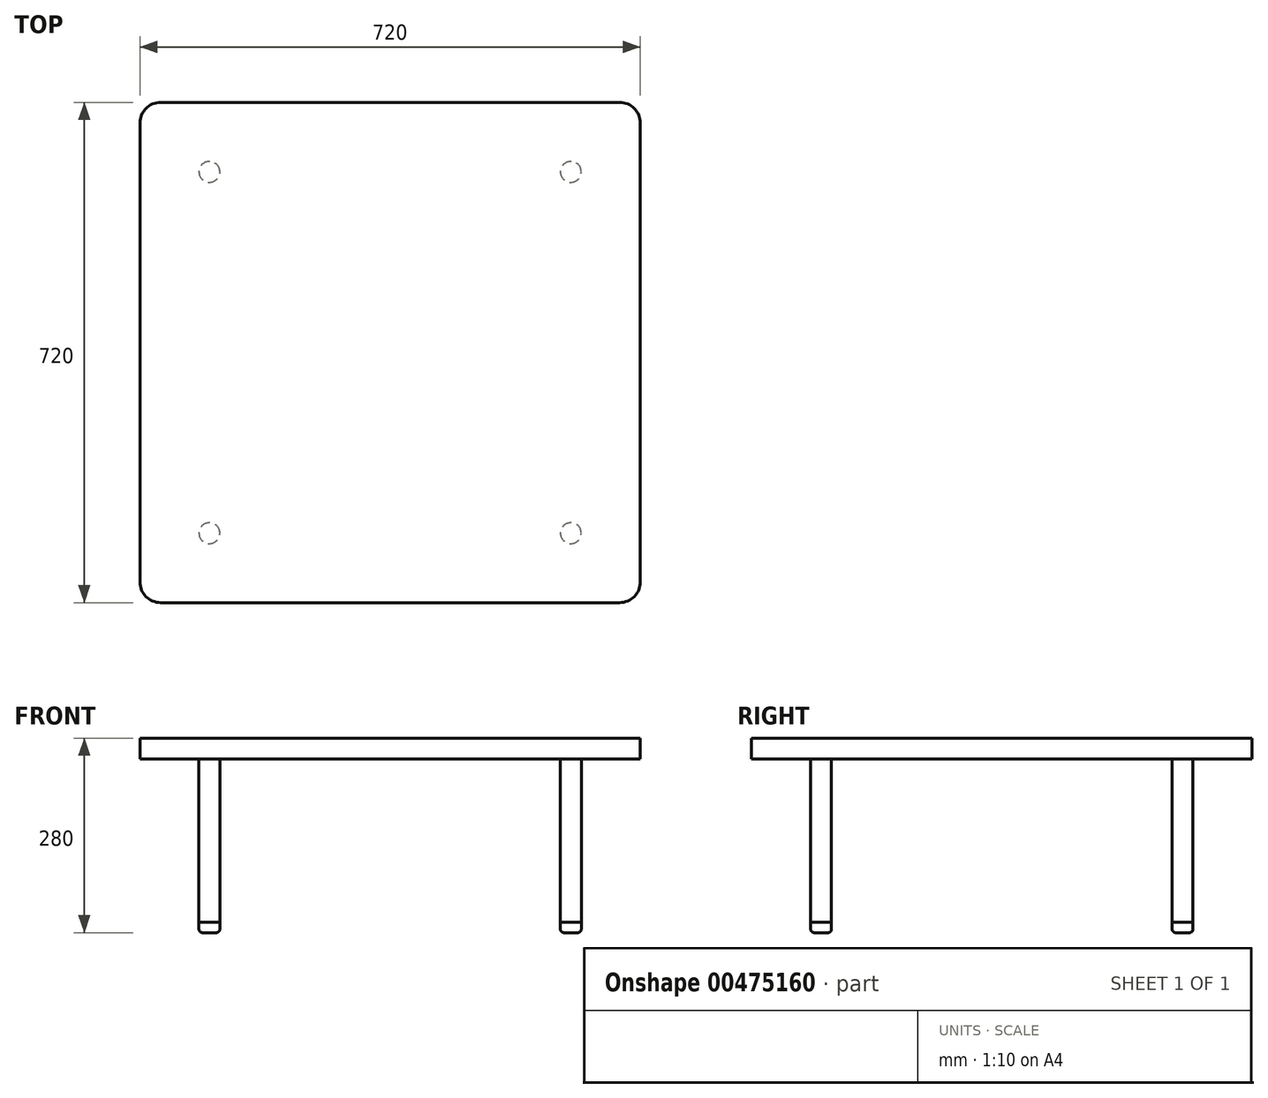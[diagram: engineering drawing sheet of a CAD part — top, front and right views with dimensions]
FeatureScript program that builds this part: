
annotation { "Feature Type Name" : "Feature", "Feature Type Description" : "" }
export const myFeature = defineFeature(function(context is Context, id is Id, definition is map)
    precondition{}
    {
        {
            var Q0;
            Q0=qCreatedBy(makeId("Top.planeOp"),FACE);
            var sketch = newSketch(context, id + "F0", { "sketchPlane" : qUnion([Q0])});
            skLineSegment(sketch, "E0.bottom", {"start": v(-360, 360) * mm, "end": v(360, 360) * mm});
            skLineSegment(sketch, "E0.top", {"start": v(-360, -360) * mm, "end": v(360, -360) * mm});
            skLineSegment(sketch, "E0.left", {"start": v(-360, 360) * mm, "end": v(-360, -360) * mm});
            skLineSegment(sketch, "E0.right", {"start": v(360, 360) * mm, "end": v(360, -360) * mm});
            skSolve(sketch);
        }
        {
            var Q0;
            Q0 = qSketchRegion(id + "F0", true);
            extrude(context, id + "F1", {"entities" : qUnion([Q0]), "depth" : 30 * mm, "offsetDistance" : 25 * mm});
        }
        {
            var Q0;
            Q0=makeQuery(id+"F1.opExtrude","SWEPT_EDGE",EDGE,{"disambiguationData":[OSD([sQuery(id+"F0.wireOp",EDGE,"E0.top"),sQuery(id+"F0.wireOp",EDGE,"E0.left")])]});
            var Q1;
            Q1=makeQuery(id+"F1.opExtrude","SWEPT_EDGE",EDGE,{"disambiguationData":[OSD([sQuery(id+"F0.wireOp",EDGE,"E0.top"),sQuery(id+"F0.wireOp",EDGE,"E0.right")])]});
            var Q2;
            Q2=makeQuery(id+"F1.opExtrude","SWEPT_EDGE",EDGE,{"disambiguationData":[OSD([sQuery(id+"F0.wireOp",EDGE,"E0.bottom"),sQuery(id+"F0.wireOp",EDGE,"E0.right")])]});
            var Q3;
            Q3=makeQuery(id+"F1.opExtrude","SWEPT_EDGE",EDGE,{"disambiguationData":[OSD([sQuery(id+"F0.wireOp",EDGE,"E0.bottom"),sQuery(id+"F0.wireOp",EDGE,"E0.left")])]});
            fillet(context, id + "F2", {"entities" : qUnion([Q0, Q1, Q2, Q3]), "radius" : 30 * mm, "tangentPropagation" : true, "allowEdgeOverflow" : false});
        }
        {
            var Q0;
            Q0=makeQuery(id+"F1.opExtrude","CAP_FACE",FACE,{"disambiguationData":[OSD([sQuery(id+"F0.wireOp",EDGE,"E0.bottom"),sQuery(id+"F0.wireOp",EDGE,"E0.top"),sQuery(id+"F0.wireOp",EDGE,"E0.left"),sQuery(id+"F0.wireOp",EDGE,"E0.right")])],"isStart":true});
            var sketch = newSketch(context, id + "F3", { "sketchPlane" : qUnion([Q0])});
            skCircle(sketch, "E1", {"center": v(260, 260) * mm, "radius": 15 * mm});
            skCircle(sketch, "E2", {"center": v(-260, 260) * mm, "radius": 15 * mm});
            skCircle(sketch, "E3", {"center": v(-260, -260) * mm, "radius": 15 * mm});
            skCircle(sketch, "E4", {"center": v(260, -260) * mm, "radius": 15 * mm});
            skSolve(sketch);
        }
        {
            var Q0;
            Q0 = qSketchRegion(id + "F3", true);
            extrude(context, id + "F4", {"entities" : qUnion([Q0]), "depth" : 235 * mm, "offsetDistance" : 25 * mm});
        }
        {
            var Q0;
            Q0=makeQuery(id+"F4.opExtrude","CAP_FACE",FACE,{"disambiguationData":[OSD([sQuery(id+"F3.wireOp",EDGE,"E2")])],"isStart":false});
            var sketch = newSketch(context, id + "F5", { "sketchPlane" : qUnion([Q0])});
            skCircle(sketch, "E5", {"center": v(-260, 260) * mm, "radius": 15 * mm});
            skCircle(sketch, "E6", {"center": v(260, 260) * mm, "radius": 15 * mm});
            skCircle(sketch, "E7", {"center": v(260, -260) * mm, "radius": 15 * mm});
            skCircle(sketch, "E8", {"center": v(-260, -260) * mm, "radius": 15 * mm});
            skSolve(sketch);
        }
        {
            var Q0;
            Q0 = qSketchRegion(id + "F5", true);
            extrude(context, id + "F6", {"entities" : qUnion([Q0]), "depth" : 15 * mm, "offsetDistance" : 25 * mm});
        }
        {
            var Q0;
            Q0=makeQuery(id+"F6.opExtrude","CAP_EDGE",EDGE,{"disambiguationData":[OSD([sQuery(id+"F5.wireOp",EDGE,"E5")])],"isStart":false});
            var Q1;
            Q1=makeQuery(id+"F6.opExtrude","CAP_EDGE",EDGE,{"disambiguationData":[OSD([sQuery(id+"F5.wireOp",EDGE,"E8")])],"isStart":false});
            var Q2;
            Q2=makeQuery(id+"F6.opExtrude","CAP_EDGE",EDGE,{"disambiguationData":[OSD([sQuery(id+"F5.wireOp",EDGE,"E7")])],"isStart":false});
            var Q3;
            Q3=makeQuery(id+"F6.opExtrude","CAP_EDGE",EDGE,{"disambiguationData":[OSD([sQuery(id+"F5.wireOp",EDGE,"E6")])],"isStart":false});
            fillet(context, id + "F7", {"entities" : qUnion([Q0, Q1, Q2, Q3]), "radius" : 5 * mm, "tangentPropagation" : true, "allowEdgeOverflow" : false});
        }
    });
